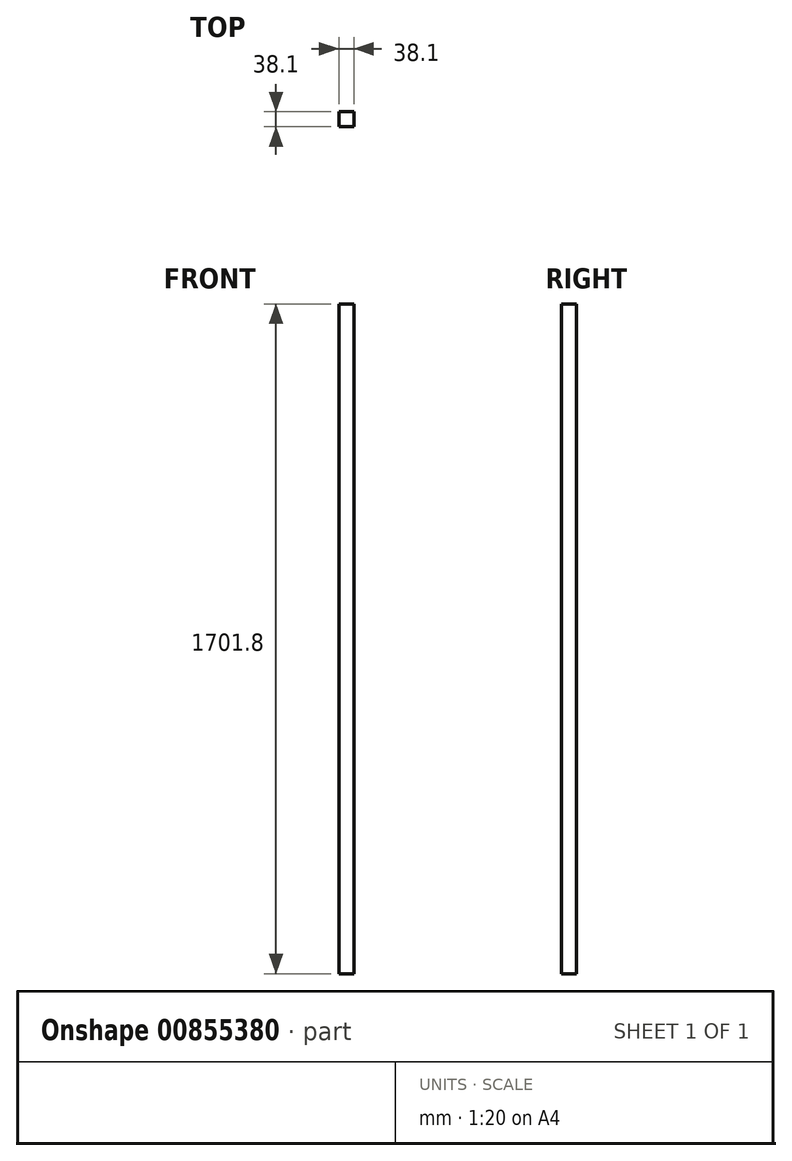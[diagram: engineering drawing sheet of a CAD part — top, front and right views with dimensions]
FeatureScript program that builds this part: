
annotation { "Feature Type Name" : "Feature", "Feature Type Description" : "" }
export const myFeature = defineFeature(function(context is Context, id is Id, definition is map)
    precondition{}
    {
        {
            var Q0;
            Q0=qCreatedBy(makeId("Top.planeOp"),FACE);
            var sketch = newSketch(context, id + "F0", { "sketchPlane" : qUnion([Q0])});
            skLineSegment(sketch, "E0.bottom", {"start": v(0, 0) * mm, "end": v(38.1, 0) * mm});
            skLineSegment(sketch, "E0.top", {"start": v(0, 38.1) * mm, "end": v(38.1, 38.1) * mm});
            skLineSegment(sketch, "E0.left", {"start": v(0, 0) * mm, "end": v(0, 38.1) * mm});
            skLineSegment(sketch, "E0.right", {"start": v(38.1, 0) * mm, "end": v(38.1, 38.1) * mm});
            skSolve(sketch);
        }
        {
            var Q0;
            Q0 = qSketchRegion(id + "F0", true);
            extrude(context, id + "F1", {"entities" : qUnion([Q0]), "depth" : 1701.8 * mm, "offsetDistance" : 25.4 * mm});
        }
    });
